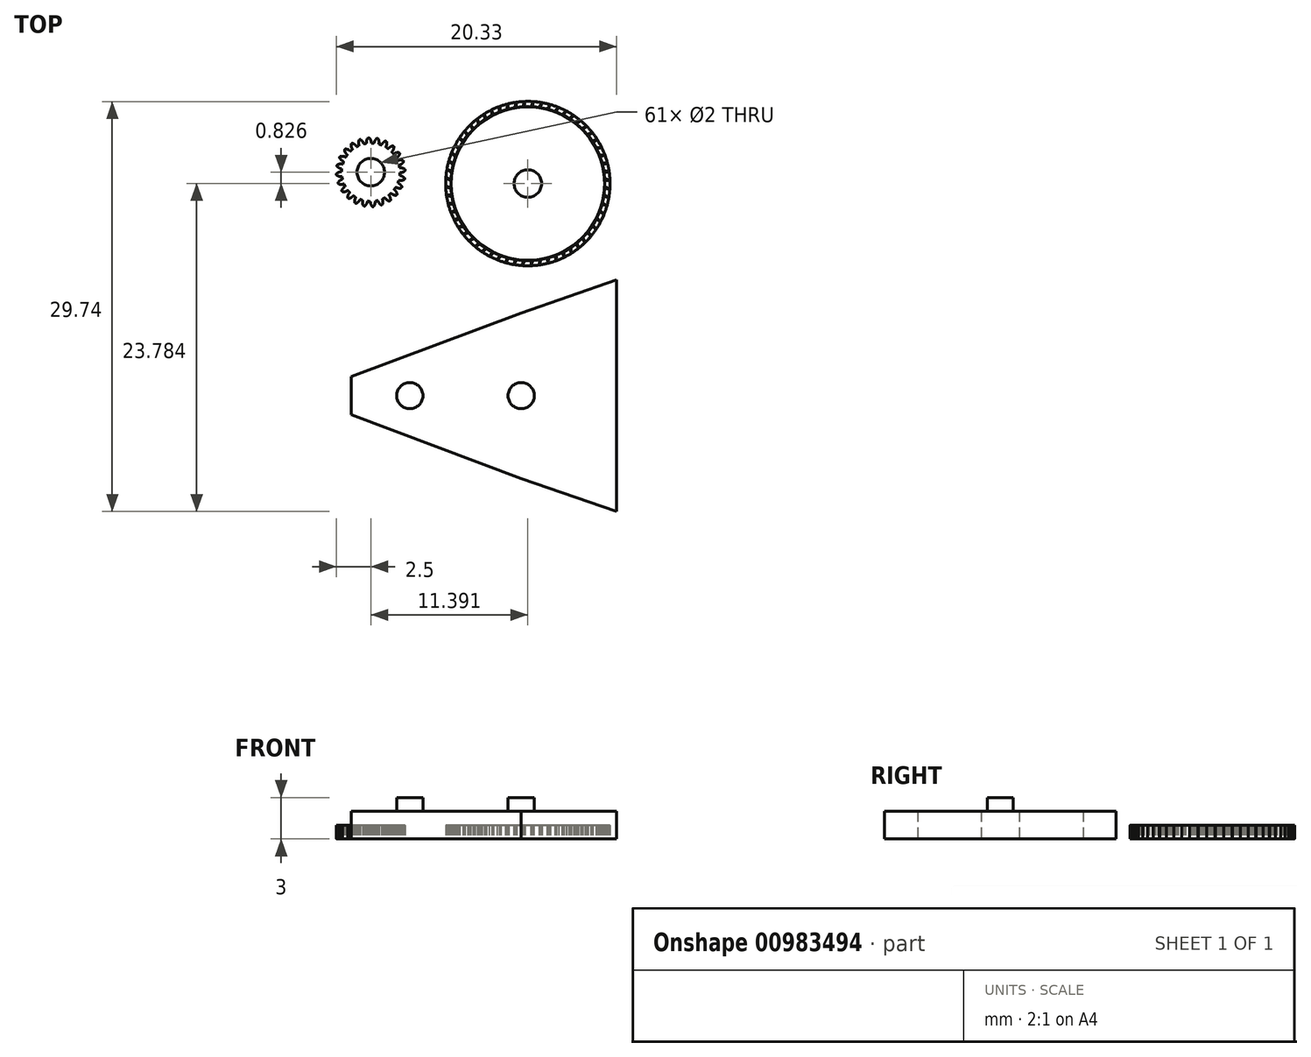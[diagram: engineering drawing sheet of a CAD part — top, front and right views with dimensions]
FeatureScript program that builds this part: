
annotation { "Feature Type Name" : "Feature", "Feature Type Description" : "" }
export const myFeature = defineFeature(function(context is Context, id is Id, definition is map)
    precondition{}
    {
        {
            var Q0;
            Q0=qCreatedBy(makeId("Top.planeOp"),FACE);
            var sketch = newSketch(context, id + "F0", { "sketchPlane" : qUnion([Q0])});
            skCircle(sketch, "E0", {"center": v(0, 0) * mm, "radius": 2.12 * mm});
            skCircle(sketch, "E1", {"center": v(0, 0) * mm, "radius": 2.31 * mm, "construction": true});
            skCircle(sketch, "E2", {"center": v(0, 0) * mm, "radius": 2.5 * mm, "construction": true});
            skLineSegment(sketch, "E3", {"start": v(0, 0) * mm, "end": v(0, 3.8) * mm, "construction": true});
            skLineSegment(sketch, "E4", {"start": v(0, 0) * mm, "end": v(-0.25, 3.84) * mm, "construction": true});
            skLineSegment(sketch, "E5", {"start": v(0, 2.31) * mm, "end": v(-2.4, 2.31) * mm, "construction": true});
            skLineSegment(sketch, "E6", {"start": v(0, 2.31) * mm, "end": v(-2.32, 1.47) * mm, "construction": true});
            skCircle(sketch, "E7", {"center": v(0, 2.31) * mm, "radius": 0.57 * mm, "construction": true});
            skCircle(sketch, "E8", {"center": v(0, 0) * mm, "radius": 2.17 * mm, "construction": true});
            skCircle(sketch, "E9", {"center": v(-0.54, 2.1) * mm, "radius": 0.57 * mm, "construction": true});
            skArc(sketch, "E10", {"start": v(0, 2.31) * mm, "mid": v(-0.05, 2.4) * mm, "end": v(-0.12, 2.5) * mm});
            skArc(sketch, "E11", {"start": v(0.04, 2.11) * mm, "mid": v(0.03, 2.21) * mm, "end": v(0, 2.31) * mm});
            skArc(sketch, "E12.MirrorCS", {"start": v(-0.3, 2.3) * mm, "mid": v(-0.27, 2.4) * mm, "end": v(-0.2, 2.5) * mm});
            skArc(sketch, "E13.MirrorCS", {"start": v(-0.31, 2.1) * mm, "mid": v(-0.32, 2.2) * mm, "end": v(-0.3, 2.3) * mm});
            skArc(sketch, "E14", {"start": v(-0.2, 2.5) * mm, "mid": v(-0.16, 2.5) * mm, "end": v(-0.12, 2.5) * mm});
            skCircle(sketch, "E15", {"center": v(0, 0) * mm, "radius": 1 * mm});
            skSolve(sketch);
        }
        {
            var Q0;
            Q0 = qSketchRegion(id + "F0", true);
            extrude(context, id + "F1", {"entities" : qUnion([Q0]), "depth" : 1 * mm, "offsetDistance" : 25 * mm});
        }
        {
            var Q0;
            Q0=makeQuery(id+"F1.opExtrude","SWEPT_BODY",BODY,{"disambiguationData":[OSD([sQuery(id+"F0.wireOp",EDGE,"E0"),sQuery(id+"F0.wireOp",EDGE,"E10"),sQuery(id+"F0.wireOp",EDGE,"E11"),sQuery(id+"F0.wireOp",EDGE,"E12.MirrorCS"),sQuery(id+"F0.wireOp",EDGE,"E13.MirrorCS"),sQuery(id+"F0.wireOp",EDGE,"E14")])]});
            var Q1;
            Q1=makeQuery(id+"F1.opExtrude","SWEPT_FACE",FACE,{"disambiguationData":[OSD([sQuery(id+"F0.wireOp",EDGE,"E0")])]});
            circularPattern(context, id + "F2", {"operationType" : NewBodyOperationType.ADD, "entities" : qUnion([Q0]), "axis" : qUnion([Q1]), "angle" : 15 * degree, "instanceCount" : 24});
        }
        {
            var Q0;
            Q0=qCreatedBy(makeId("Top.planeOp"),FACE);
            var sketch = newSketch(context, id + "F3", { "sketchPlane" : qUnion([Q0])});
            skCircle(sketch, "E16", {"center": v(11.4, -0.83) * mm, "radius": 5.96 * mm});
            skCircle(sketch, "E17", {"center": v(11.4, -0.83) * mm, "radius": 5.77 * mm, "construction": true});
            skCircle(sketch, "E18", {"center": v(11.4, -0.83) * mm, "radius": 5.58 * mm});
            skLineSegment(sketch, "E19", {"start": v(11.4, -0.83) * mm, "end": v(11.4, 9.13) * mm, "construction": true});
            skLineSegment(sketch, "E20", {"start": v(11.4, -0.83) * mm, "end": v(11.12, 9.44) * mm, "construction": true});
            skLineSegment(sketch, "E21", {"start": v(11.4, 4.94) * mm, "end": v(6.58, 4.94) * mm, "construction": true});
            skLineSegment(sketch, "E22", {"start": v(11.4, 4.94) * mm, "end": v(6.81, 3.28) * mm, "construction": true});
            skCircle(sketch, "E23", {"center": v(11.4, -0.83) * mm, "radius": 5.42 * mm, "construction": true});
            skCircle(sketch, "E24", {"center": v(11.4, 4.94) * mm, "radius": 1.44 * mm});
            skCircle(sketch, "E25", {"center": v(10.05, 4.43) * mm, "radius": 1.44 * mm});
            skArc(sketch, "E26", {"start": v(11.4, 4.94) * mm, "mid": v(11.31, 5.1) * mm, "end": v(11.23, 5.25) * mm});
            skArc(sketch, "E27", {"start": v(11.45, 4.75) * mm, "mid": v(11.43, 4.85) * mm, "end": v(11.4, 4.94) * mm});
            skArc(sketch, "E28.MirrorCS", {"start": v(11.09, 4.94) * mm, "mid": v(11.16, 5.1) * mm, "end": v(11.23, 5.25) * mm});
            skArc(sketch, "E29.MirrorCS", {"start": v(11.04, 4.74) * mm, "mid": v(11.06, 4.84) * mm, "end": v(11.09, 4.94) * mm});
            skCircle(sketch, "E30", {"center": v(11.4, -0.83) * mm, "radius": 1 * mm});
            skSolve(sketch);
        }
        {
            var Q0;
            {var subQ0=sQuery(id+"F3.wireOp",EDGE,"E24");var subQ1=sQuery(id+"F3.wireOp",EDGE,"E18");var subQ2=makeQuery(id+"F3.imprint","INTERSECT",VERTEX,{"disambiguationData":[OD(0.0)],"derivedFrom":[subQ1,subQ0]});Q0=makeQuery(id+"F3.imprint","IMPRINT",FACE,{"disambiguationData":[TD([[makeQuery(id+"F3.imprint","IMPRINT",EDGE,{"disambiguationData":[TD([[subQ2,1.0]])],"derivedFrom":subQ1}),1.0]])]});}
            var Q1;
            {var subQ8=sQuery(id+"F3.wireOp",EDGE,"E29.MirrorCS");Q1=makeQuery(id+"F3.imprint","IMPRINT",FACE,{"disambiguationData":[TD([[makeQuery(id+"F3.imprint","IMPRINT",EDGE,{"derivedFrom":subQ8}),-1.0]])]});}
            var Q2;
            {var subQ1=sQuery(id+"F3.wireOp",EDGE,"E18");var subQ3=sQuery(id+"F3.wireOp",EDGE,"E24");var subQ4=makeQuery(id+"F3.imprint","INTERSECT",VERTEX,{"disambiguationData":[OD(0.0)],"derivedFrom":[subQ1,subQ3]});Q2=makeQuery(id+"F3.imprint","IMPRINT",FACE,{"disambiguationData":[TD([[makeQuery(id+"F3.imprint","IMPRINT",EDGE,{"disambiguationData":[TD([[subQ4,1.0]])],"derivedFrom":subQ3}),1.0]])]});}
            var Q3;
            {var subQ1=sQuery(id+"F3.wireOp",EDGE,"E18");var subQ3=makeQuery(id+"F3.imprint","INTERSECT",VERTEX,{"derivedFrom":[subQ1,sQuery(id+"F3.wireOp",EDGE,"E29.MirrorCS")]});Q3=makeQuery(id+"F3.imprint","IMPRINT",FACE,{"disambiguationData":[TD([[makeQuery(id+"F3.imprint","IMPRINT",EDGE,{"disambiguationData":[TD([[subQ3,-1.0]])],"derivedFrom":subQ1}),1.0]])]});}
            var Q4;
            {var subQ0=sQuery(id+"F3.wireOp",EDGE,"E24");var subQ1=sQuery(id+"F3.wireOp",EDGE,"E18");var subQ2=makeQuery(id+"F3.imprint","INTERSECT",VERTEX,{"disambiguationData":[OD(1.0)],"derivedFrom":[subQ1,subQ0]});Q4=makeQuery(id+"F3.imprint","IMPRINT",FACE,{"disambiguationData":[TD([[makeQuery(id+"F3.imprint","IMPRINT",EDGE,{"disambiguationData":[TD([[subQ2,-1.0]])],"derivedFrom":subQ1}),1.0]])]});}
            extrude(context, id + "F4", {"entities" : qUnion([Q0, Q1, Q2, Q3, Q4]), "depth" : 1 * mm, "offsetDistance" : 25 * mm});
        }
        {
            var Q0;
            Q0=makeQuery(id+"F4.opExtrude","SWEPT_BODY",BODY,{"disambiguationData":[OSD([sQuery(id+"F3.wireOp",EDGE,"E18"),sQuery(id+"F3.wireOp",EDGE,"E26"),sQuery(id+"F3.wireOp",EDGE,"E27"),sQuery(id+"F3.wireOp",EDGE,"E28.MirrorCS"),sQuery(id+"F3.wireOp",EDGE,"E29.MirrorCS")])]});
            var Q1;
            Q1=makeQuery(id+"F4.opExtrude","SWEPT_FACE",FACE,{"disambiguationData":[OSD([sQuery(id+"F3.wireOp",EDGE,"E18")])]});
            circularPattern(context, id + "F5", {"operationType" : NewBodyOperationType.ADD, "entities" : qUnion([Q0]), "axis" : qUnion([Q1]), "angle" : 6 * degree, "instanceCount" : 60});
        }
        {
            var Q0;
            Q0=qCreatedBy(makeId("Top.planeOp"),FACE);
            var sketch = newSketch(context, id + "F6", { "sketchPlane" : qUnion([Q0])});
            skCircle(sketch, "E31", {"center": v(10.91, -16.2) * mm, "radius": 0.95 * mm});
            skCircle(sketch, "E32", {"center": v(2.83, -16.2) * mm, "radius": 0.95 * mm});
            skPoint(sketch, "E33", {"position": v(10.91, -10.2) * mm});
            skPoint(sketch, "E34", {"position": v(2.83, -13.2) * mm});
            skLineSegment(sketch, "E35", {"start": v(-6.47, -16.2) * mm, "end": v(26.96, -16.2) * mm, "construction": true});
            skLineSegment(sketch, "E36", {"start": v(10.91, -10.2) * mm, "end": v(-1.42, -14.82) * mm});
            skLineSegment(sketch, "E37", {"start": v(-1.42, -14.82) * mm, "end": v(-1.42, -16.2) * mm});
            skLineSegment(sketch, "E38", {"start": v(10.91, -10.2) * mm, "end": v(17.83, -7.8) * mm});
            skLineSegment(sketch, "E39", {"start": v(17.83, -7.8) * mm, "end": v(17.83, -16.2) * mm});
            skLineSegment(sketch, "E40.MirrorCS", {"start": v(10.91, -22.2) * mm, "end": v(-1.42, -17.6) * mm});
            skLineSegment(sketch, "E41.MirrorCS", {"start": v(10.91, -22.2) * mm, "end": v(17.83, -24.6) * mm});
            skLineSegment(sketch, "E42.MirrorCS", {"start": v(17.83, -24.6) * mm, "end": v(17.83, -16.2) * mm});
            skLineSegment(sketch, "E43.MirrorCS", {"start": v(-1.42, -17.6) * mm, "end": v(-1.42, -16.2) * mm});
            skSolve(sketch);
        }
        {
            var Q0;
            Q0=makeQuery(id+"F6.imprint","IMPRINT",FACE,{"disambiguationData":[TD([[makeQuery(id+"F6.imprint","IMPRINT",EDGE,{"derivedFrom":sQuery(id+"F6.wireOp",EDGE,"E31")}),-1.0]])]});
            extrude(context, id + "F7", {"entities" : qUnion([Q0]), "depth" : 2 * mm, "offsetDistance" : 25 * mm});
        }
        {
            var Q0;
            Q0=makeQuery(id+"F6.imprint","IMPRINT",FACE,{"disambiguationData":[TD([[makeQuery(id+"F6.imprint","IMPRINT",EDGE,{"derivedFrom":sQuery(id+"F6.wireOp",EDGE,"E32")}),1.0]])]});
            var Q1;
            Q1=makeQuery(id+"F6.imprint","IMPRINT",FACE,{"disambiguationData":[TD([[makeQuery(id+"F6.imprint","IMPRINT",EDGE,{"derivedFrom":sQuery(id+"F6.wireOp",EDGE,"E31")}),1.0]])]});
            extrude(context, id + "F8", {"entities" : qUnion([Q0, Q1]), "operationType" : NewBodyOperationType.ADD, "depth" : 3 * mm, "offsetDistance" : 25 * mm});
        }
    });
